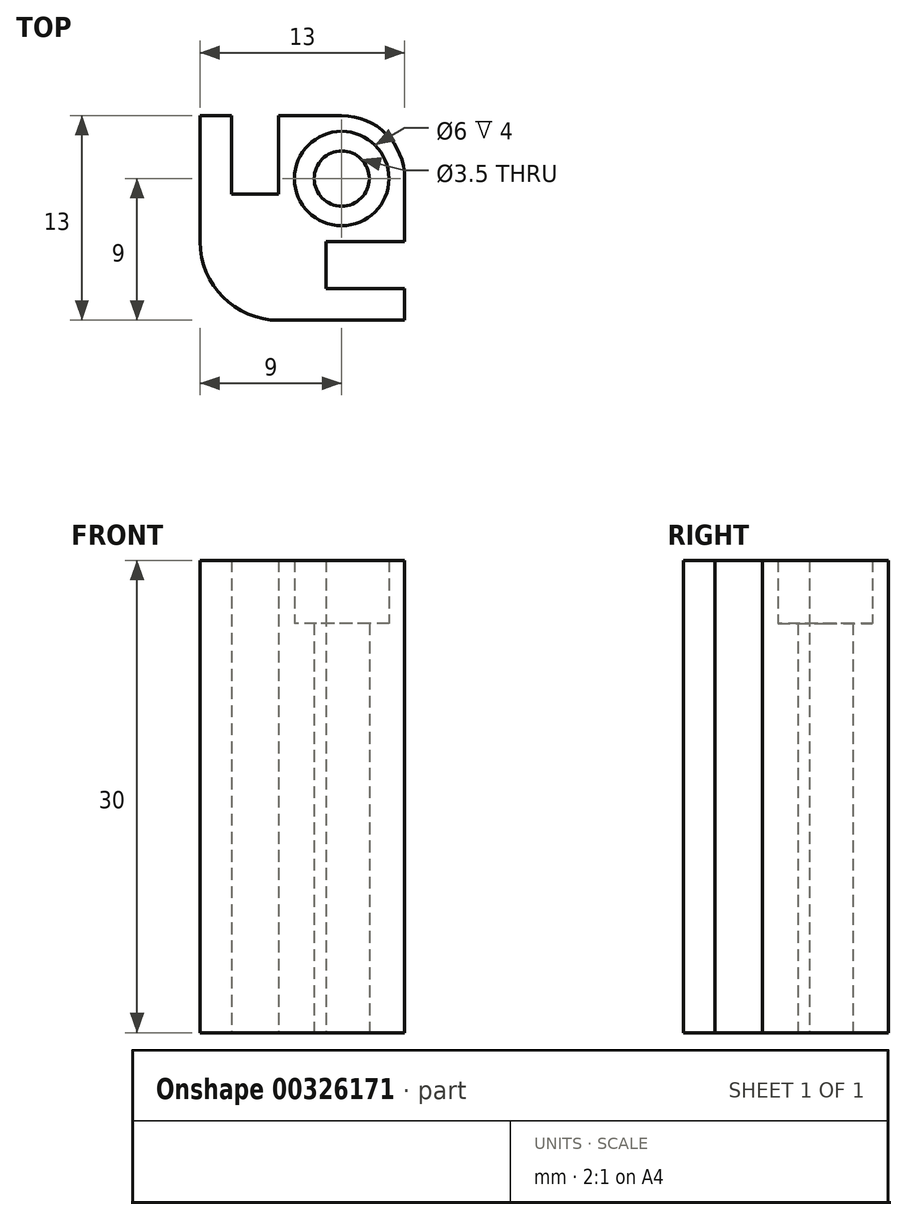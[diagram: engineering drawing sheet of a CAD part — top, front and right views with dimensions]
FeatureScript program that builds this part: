
annotation { "Feature Type Name" : "Feature", "Feature Type Description" : "" }
export const myFeature = defineFeature(function(context is Context, id is Id, definition is map)
    precondition{}
    {
        {
            var Q0;
            Q0=qCreatedBy(makeId("Top.planeOp"),FACE);
            var sketch = newSketch(context, id + "F0", { "sketchPlane" : qUnion([Q0])});
            skCircle(sketch, "E0", {"center": v(-60, 60) * mm, "radius": 1.75 * mm});
            skCircle(sketch, "E1.0.1.0", {"center": v(-60, -60) * mm, "radius": 1.75 * mm});
            skCircle(sketch, "E1.1.0.0", {"center": v(60, 60) * mm, "radius": 1.75 * mm});
            skCircle(sketch, "E1.1.1.0", {"center": v(60, -60) * mm, "radius": 1.75 * mm});
            skLineSegment(sketch, "E1.direction1", {"start": v(-60, 60) * mm, "end": v(60, 60) * mm, "construction": true});
            skLineSegment(sketch, "E1.direction2", {"start": v(-60, 60) * mm, "end": v(-60, -60) * mm, "construction": true});
            skCircle(sketch, "E2", {"center": v(-60, -60) * mm, "radius": 4 * mm});
            skCircle(sketch, "E3", {"center": v(-60, -60) * mm, "radius": 3 * mm});
            skLineSegment(sketch, "E4.bottom", {"start": v(-56, -64) * mm, "end": v(-61, -64) * mm});
            skLineSegment(sketch, "E4.top", {"start": v(-60, -56) * mm, "end": v(-64, -56) * mm});
            skLineSegment(sketch, "E4.left", {"start": v(-56, -64) * mm, "end": v(-56, -60) * mm});
            skLineSegment(sketch, "E4.right", {"start": v(-64, -61) * mm, "end": v(-64, -56) * mm});
            skPoint(sketch, "E5.orphan", {"position": v(-56, -56) * mm});
            skLineSegment(sketch, "E6", {"start": v(-64, -69) * mm, "end": v(-64, -69) * mm});
            skLineSegment(sketch, "E7", {"start": v(-69, -64) * mm, "end": v(-69, -56) * mm});
            skLineSegment(sketch, "E8", {"start": v(-69, -56) * mm, "end": v(-67, -56) * mm});
            skLineSegment(sketch, "E9", {"start": v(-67, -56) * mm, "end": v(-67, -61) * mm});
            skLineSegment(sketch, "E10", {"start": v(-64, -69) * mm, "end": v(-56, -69) * mm});
            skLineSegment(sketch, "E11", {"start": v(-56, -69) * mm, "end": v(-56, -67) * mm});
            skLineSegment(sketch, "E12", {"start": v(-56, -67) * mm, "end": v(-61, -67) * mm});
            skLineSegment(sketch, "E13", {"start": v(-61, -67) * mm, "end": v(-61, -64) * mm});
            skLineSegment(sketch, "E14", {"start": v(-64, -61) * mm, "end": v(-67, -61) * mm});
            skPoint(sketch, "E15.start.orphan", {"position": v(-67, -64) * mm});
            skPoint(sketch, "E16.start.orphan", {"position": v(-64, -67) * mm});
            skPoint(sketch, "E17.orphan", {"position": v(-64, -64) * mm});
            skPoint(sketch, "E18.visualSharp", {"position": v(-69, -69) * mm});
            skArc(sketch, "E18.filletArc", {"start": v(-69, -64) * mm, "mid": v(-67.54, -67.54) * mm, "end": v(-64, -69) * mm});
            skSolve(sketch);
        }
        {
            var Q0;
            Q0=makeQuery(id+"F0.imprint","IMPRINT",FACE,{"disambiguationData":[TD([[makeQuery(id+"F0.imprint","IMPRINT",EDGE,{"derivedFrom":sQuery(id+"F0.wireOp",EDGE,"E2")}),1.0]])]});
            var Q1;
            {var subQ0=sQuery(id+"F0.wireOp",EDGE,"E4.top");Q1=makeQuery(id+"F0.imprint","IMPRINT",FACE,{"disambiguationData":[TD([[makeQuery(id+"F0.imprint","IMPRINT",EDGE,{"derivedFrom":subQ0}),1.0]])]});}
            var Q2;
            {var subQ0=sQuery(id+"F0.wireOp",EDGE,"E4.right");var subQ1=sQuery(id+"F0.wireOp",EDGE,"E2");var subQ2=makeQuery(id+"F0.imprint","INTERSECT",VERTEX,{"derivedFrom":[subQ1,subQ0]});Q2=makeQuery(id+"F0.imprint","IMPRINT",FACE,{"disambiguationData":[TD([[makeQuery(id+"F0.imprint","IMPRINT",EDGE,{"disambiguationData":[TD([[subQ2,-1.0]])],"derivedFrom":subQ1}),-1.0]])]});}
            var Q3;
            {var subQ0=sQuery(id+"F0.wireOp",EDGE,"E4.left");Q3=makeQuery(id+"F0.imprint","IMPRINT",FACE,{"disambiguationData":[TD([[makeQuery(id+"F0.imprint","IMPRINT",EDGE,{"derivedFrom":subQ0}),1.0]])]});}
            extrude(context, id + "F1", {"entities" : qUnion([Q0, Q1, Q2, Q3]), "depth" : 30 * mm});
        }
        {
            var Q0;
            Q0=makeQuery(id+"F0.imprint","IMPRINT",FACE,{"disambiguationData":[TD([[makeQuery(id+"F0.imprint","IMPRINT",EDGE,{"derivedFrom":sQuery(id+"F0.wireOp",EDGE,"E1.0.1.0")}),-1.0]])]});
            extrude(context, id + "F2", {"entities" : qUnion([Q0]), "operationType" : NewBodyOperationType.ADD, "depth" : 26 * mm});
        }
    });
